# Revit family: 11462_v1
name_source: partatom
category: Systemy meblowe
units: mm (PartAtom-declared; Revit-internal decimal feet)

## family parameters
Oparty na płaszczyźnie roboczej = Nie
Punkt obliczania pomieszczeń = Nie
Tnij formami wycięć po wczytaniu = Nie
Typ części = Normalny
Współdzielony = Nie
Wymiar okrągłego złącza = Użyj średnicy
Włącz cięcie w widokach = Nie
Zawsze pionowo = Tak

## types (1)
- 11462_v1
    Base material = Wood, 
Larch wood, Stainless steel, Powder coated steel, Reinforced ropes (PP-Polypropylene), Soft rope (PP-Polypropylene), Fiberglass, Steel plates covered in plastisol, Anti-slip, Waterproof Plywood, HDPE
    Critical falling height = 236 cm
    Domyślna rzędna = 0 cm
    Height = 319 cm
    Hosted on larslaj.com = https://larslaj.com
    LARSLAJ_materials = larslaj.com/bim
    Lenght = 689 cm
    Maintenance of acacia = We recommend to examine and tighten all screws and bolt clamps after a
few weeks’ use. In order to prevent cracks and to extend the life of the
wood, it is recommended that the wood details should be oiled every 3-5
years.
    Maintenance of larch = We recommend to examine and tighten all screws and bolt clamps after a
few weeks’ use. All wooden playground elements should be preserved with
transparent impregnating oil such as: wood preservation, or other
similar impregnating oil, safe for children at least once a year,
depending on local climate conditions (exposure to sunlight or rainfall).
    Maintenance of metal devices,rocking and seesaw = We recommend to examine and tighten all screws and bolt clamps after a
few weeks’ use.
    Model = 11462
    Producent = Lars Laj
    Product line = Pioneer
    Product name = Vilcabamba
    Safety zone = 998x885 cm
    Steel = <Wg kategorii>
    URL = https://www.larslaj.com
    Width = 604 cm
    Wood = <Wg kategorii>
